# Revit family: 2059339 Sylvania Lighting Fixture MC2 D I 2-4M 4K DALIEM WHT PRIS
name_source: partatom
category: Lighting Fixtures
revit_build: Autodesk Revit 2016 (Build: 20150220_1215(x64)
units: mm (PartAtom-declared; Revit-internal decimal feet)

## family parameters
Cut with Voids When Loaded = No
Host = Face
Light Source = Yes
OmniClass Number = 23.80.70.11.17
OmniClass Title = Specialized Lighting by Location or Use
Part Type = Normal
Room Calculation Point = No
Round Connector Dimension = Use Diameter
Shared = No

## types (2) — shared parameters
Apparent Load = 67 VA
Assembly Code = D5020200
AssetType = Fixed
Color Filter = 16777215
Description = 2059339   MC2 D/I 2.4M 4K DALIEM WHT PRIS  Continuous lines of LED light, white RAL 9016, direct/indirect distribution (65/35), various accessories available, compact and minimalist design based on the Golden Mean, ideal for offices, meeting rooms, corridors, education facilities, museums and libraries, extruded aluminium body, diffuser: micro prismatic, colour temperature: 4000K neutral white, total system power: 67W, total fixture output: 7666lm, luminaire efficacy: 114lm/W, LOR: 100%, colour rendering: Ra >80, LED Chromacity: 1 step MacAdam ellipse, lifetime: 60,000 hours at 90% of the original output (L90), energy class: A++, A+, A, IR/UV free light source without heat radiation, operating voltage: 220-240V / 50-60Hz, drive current: (Direct) 800mA + (Indirect) 350mA, electronic driver, DALI dimmable, direct/indirect independently addressable, integral emergency: 3 hour maintained, electrical protection: CLASS I, IP20, suitable for internal environment only.
Dimming Lamp Color Temperature Shift = <None>
DocumentationLiterature = http://www.sylvania-lighting.com
DurationUnit = hours
ElectricShockClassification = Class I
Emit Shape Visible in Rendering = No
Emit from Rectangle Length = 2400 mm
Emit from Rectangle Width = 52 mm  [stored 0.170604 ft]
ExpectedLife = 50000
Height_SYL = 86 mm  [stored 0.282152 ft]
IfcExportAs = IfcLightFixtureType
IfcExportType = IfcLightFixtureType
IngressProtection = IP20
Keynote = 16500
Lamp = LED
LampColourRenderingIndex = 80
LampColourTemperature = 4000 K
LampMacAdamStep = 3
LampsType = LED
Length_SYL = 2400 mm
LightOutputRatio = 100
Manufacturer = Feilo Sylvania
ManufacturerName = Feilo Sylvania
Material = aluminium housing, polycarbonate diffuser
Material_1_SYL = Metal_Sylvania_Mini Continuum II_White
Material_2_SYL = Polycarbonate_Sylvania_Mini Continuum II_Opal_4000K
Material_3_SYL = Metal_Sylvania_Mini Contiuum II_Silver
Material_4_SYL = Metal_Sylvania_Mini Contiuum II_Silver
Model = MC2 D/I 2.4M 4K DALIEM WHT PRIS
ModelNumber = 2059339
ModelReference = MC2 D/I 2.4M 4K DALIEM WHT PRIS
NominalHeight = 86 mm  [stored 0.282152 ft]
NominalLength = 2400 mm
PowerConsumption = 67 W
PowerFactor = 0.95
Tilt Angle = -90.00°
URL = http://www.sylvania-lighting.com
Voltage = 0 V
Weight = 6.3 kg
Width_SYL = 54 mm  [stored 0.177165 ft]
zero-valued in all types: Default Elevation, NominalWidth

## per-type parameters (varying)
| type | LampNominalLuminous | LuminousEfficacy | Name | Photometric Web File | TypeName |
| 2059339 MC2 D/I 2.4M 4K DALIEM WHT PRIS Emergency mode | 121 lm | 1.805 lm/W | MC2 D/I 2.4M 4K DALIEM WHT PRIS Emergency mode | 2059339EM.ies | MC2 D/I 2.4M 4K DALIEM WHT PRIS Emergency mode |
| 2059339 MC2 D/I 2.4M 4K DALIEM WHT PRIS | 7776 lm | 116 lm/W | MC2 D/I 2.4M 4K DALIEM WHT PRIS | 2059339.ies | MC2 D/I 2.4M 4K DALIEM WHT PRIS |

note: [stored X ft] marks values corroborated as IEEE doubles in the binary element streams (Revit-internal decimal feet)

## geometry (parser evidence)
native form markers: Sweep x3
no freeform markers — native parametric forms only
